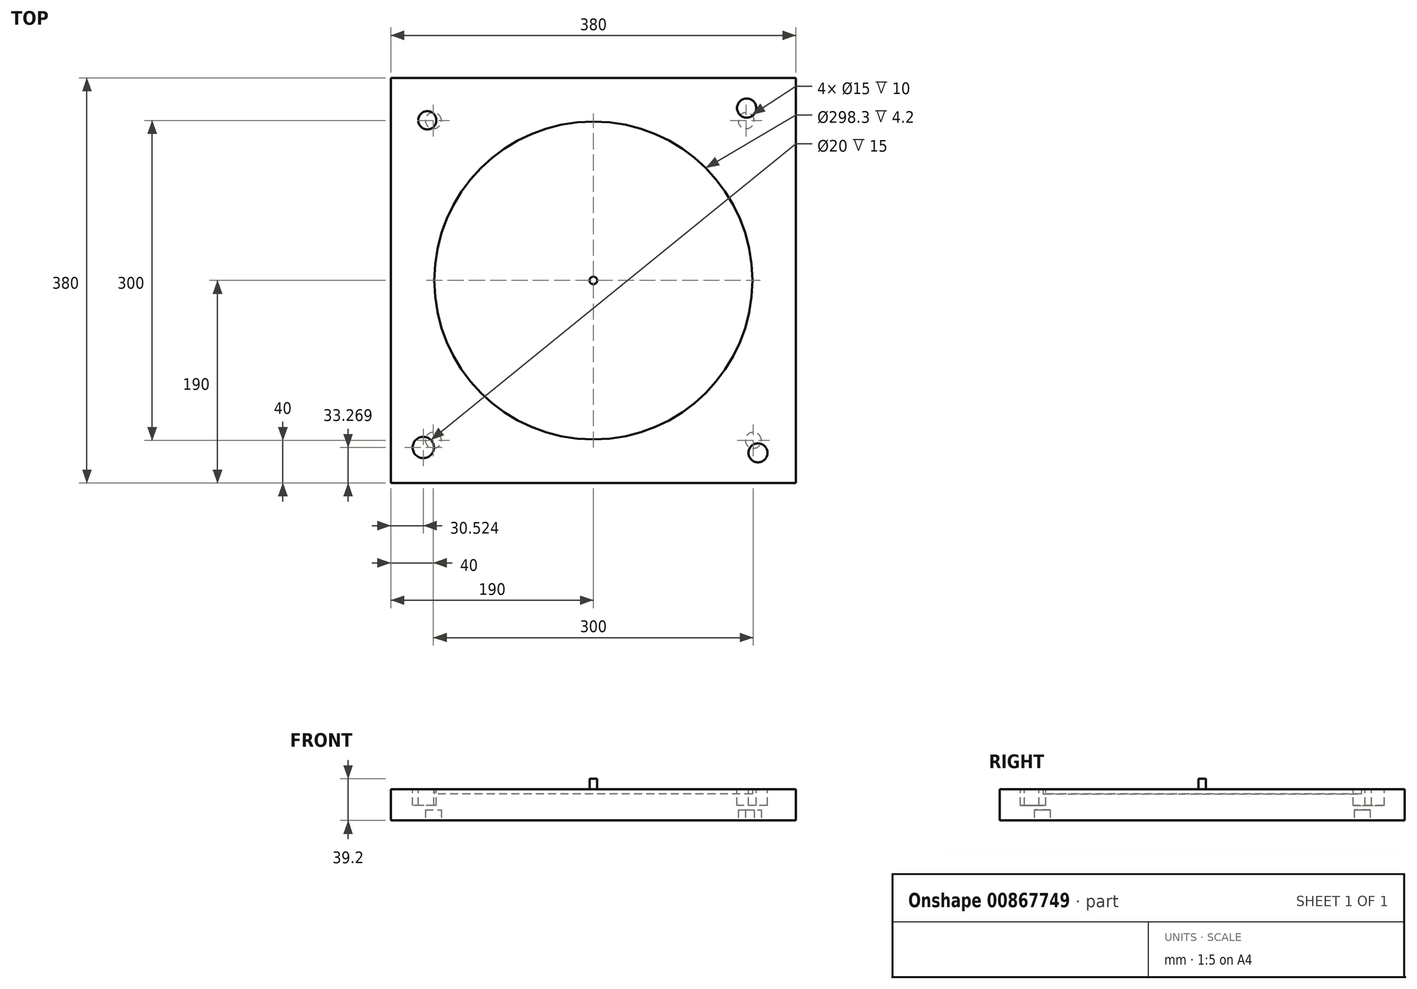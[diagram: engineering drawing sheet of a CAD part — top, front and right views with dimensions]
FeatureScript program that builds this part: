
annotation { "Feature Type Name" : "Feature", "Feature Type Description" : "" }
export const myFeature = defineFeature(function(context is Context, id is Id, definition is map)
    precondition{}
    {
        {
            var Q0;
            Q0=qCreatedBy(makeId("Top.planeOp"),FACE);
            var sketch = newSketch(context, id + "F0", { "sketchPlane" : qUnion([Q0])});
            skLineSegment(sketch, "E0.bottom", {"start": v(-190, 190) * mm, "end": v(190, 190) * mm});
            skLineSegment(sketch, "E0.top", {"start": v(-190, -190) * mm, "end": v(190, -190) * mm});
            skLineSegment(sketch, "E0.left", {"start": v(-190, 190) * mm, "end": v(-190, -190) * mm});
            skLineSegment(sketch, "E0.right", {"start": v(190, 190) * mm, "end": v(190, -190) * mm});
            skPoint(sketch, "E0.middle", {"position": v(0, 0) * mm});
            skSolve(sketch);
        }
        {
            var Q0;
            Q0=makeQuery(id+"F0.imprint","IMPRINT",FACE,{"disambiguationData":[TD([[makeQuery(id+"F0.imprint","IMPRINT",EDGE,{"derivedFrom":sQuery(id+"F0.wireOp",EDGE,"E0.bottom")}),-1.0]])]});
            var sketch = newSketch(context, id + "F1", { "sketchPlane" : qUnion([Q0])});
            skCircle(sketch, "E1", {"center": v(0, 0) * mm, "radius": 149.15 * mm});
            skCircle(sketch, "E2", {"center": v(0, 0) * mm, "radius": 3.6 * mm});
            skSolve(sketch);
        }
        {
            var Q0;
            Q0=makeQuery(id+"F0.imprint","IMPRINT",FACE,{"disambiguationData":[TD([[makeQuery(id+"F0.imprint","IMPRINT",EDGE,{"derivedFrom":sQuery(id+"F0.wireOp",EDGE,"E0.bottom")}),-1.0]])]});
            extrude(context, id + "F2", {"entities" : qUnion([Q0]), "depth" : 25 * mm, "offsetDistance" : 25 * mm});
        }
        {
            var Q0;
            Q0=makeQuery(id+"F1.imprint","IMPRINT",FACE,{"disambiguationData":[TD([[makeQuery(id+"F1.imprint","IMPRINT",EDGE,{"derivedFrom":sQuery(id+"F1.wireOp",EDGE,"E1")}),1.0]])]});
            extrude(context, id + "F3", {"entities" : qUnion([Q0]), "operationType" : NewBodyOperationType.ADD, "depth" : 4.2 * mm, "offsetDistance" : 25 * mm});
        }
        {
            var Q0;
            Q0=makeQuery(id+"F2.opExtrude","CAP_FACE",FACE,{"disambiguationData":[OSD([sQuery(id+"F0.wireOp",EDGE,"E0.bottom"),sQuery(id+"F0.wireOp",EDGE,"E0.top"),sQuery(id+"F0.wireOp",EDGE,"E0.left"),sQuery(id+"F0.wireOp",EDGE,"E0.right")])],"isStart":false});
            var sketch = newSketch(context, id + "F4", { "sketchPlane" : qUnion([Q0])});
            skCircle(sketch, "E3", {"center": v(0, 0) * mm, "radius": 149.15 * mm});
            skSolve(sketch);
        }
        {
            var Q0;
            Q0=makeQuery(id+"F4.imprint","IMPRINT",FACE,{"disambiguationData":[TD([[makeQuery(id+"F4.imprint","IMPRINT",EDGE,{"derivedFrom":sQuery(id+"F4.wireOp",EDGE,"E3")}),-1.0]])]});
            extrude(context, id + "F5", {"entities" : qUnion([Q0]), "operationType" : NewBodyOperationType.ADD, "depth" : 4.2 * mm, "offsetDistance" : 25 * mm});
        }
        {
            var Q0;
            Q0=makeQuery(id+"F5.opExtrude","CAP_FACE",FACE,{"disambiguationData":[OSD([sQuery(id+"F0.wireOp",EDGE,"E0.bottom"),sQuery(id+"F0.wireOp",EDGE,"E0.top"),sQuery(id+"F0.wireOp",EDGE,"E0.left"),sQuery(id+"F0.wireOp",EDGE,"E0.right"),sQuery(id+"F4.wireOp",EDGE,"E3")])],"isStart":false});
            var sketch = newSketch(context, id + "F6", { "sketchPlane" : qUnion([Q0])});
            skCircle(sketch, "E4", {"center": v(0, 0) * mm, "radius": 3.6 * mm});
            skSolve(sketch);
        }
        {
            var Q0;
            Q0=makeQuery(id+"F2.opExtrude","CAP_FACE",FACE,{"disambiguationData":[OSD([sQuery(id+"F0.wireOp",EDGE,"E0.bottom"),sQuery(id+"F0.wireOp",EDGE,"E0.top"),sQuery(id+"F0.wireOp",EDGE,"E0.left"),sQuery(id+"F0.wireOp",EDGE,"E0.right")])],"isStart":true});
            var sketch = newSketch(context, id + "F7", { "sketchPlane" : qUnion([Q0])});
            skCircle(sketch, "E5", {"center": v(-150, 150) * mm, "radius": 7.5 * mm});
            skCircle(sketch, "E6", {"center": v(-150, -150) * mm, "radius": 7.5 * mm});
            skCircle(sketch, "E7", {"center": v(143.27, -150) * mm, "radius": 7.5 * mm});
            skCircle(sketch, "E8", {"center": v(150, 150) * mm, "radius": 7.5 * mm});
            skSolve(sketch);
        }
        {
            var Q0;
            Q0=makeQuery(id+"F7.imprint","IMPRINT",FACE,{"disambiguationData":[TD([[makeQuery(id+"F7.imprint","IMPRINT",EDGE,{"derivedFrom":sQuery(id+"F7.wireOp",EDGE,"E5")}),1.0]])]});
            var Q1;
            Q1=makeQuery(id+"F7.imprint","IMPRINT",FACE,{"disambiguationData":[TD([[makeQuery(id+"F7.imprint","IMPRINT",EDGE,{"derivedFrom":sQuery(id+"F7.wireOp",EDGE,"E6")}),1.0]])]});
            var Q2;
            Q2=makeQuery(id+"F7.imprint","IMPRINT",FACE,{"disambiguationData":[TD([[makeQuery(id+"F7.imprint","IMPRINT",EDGE,{"derivedFrom":sQuery(id+"F7.wireOp",EDGE,"E7")}),1.0]])]});
            var Q3;
            Q3=makeQuery(id+"F7.imprint","IMPRINT",FACE,{"disambiguationData":[TD([[makeQuery(id+"F7.imprint","IMPRINT",EDGE,{"derivedFrom":sQuery(id+"F7.wireOp",EDGE,"E8")}),1.0]])]});
            extrude(context, id + "F8", {"entities" : qUnion([Q0, Q1, Q2, Q3]), "operationType" : NewBodyOperationType.REMOVE, "oppositeDirection" : true, "depth" : 10 * mm, "offsetDistance" : 25 * mm});
        }
        {
            var Q0;
            Q0=makeQuery(id+"F5.opExtrude","CAP_FACE",FACE,{"disambiguationData":[OSD([sQuery(id+"F0.wireOp",EDGE,"E0.bottom"),sQuery(id+"F0.wireOp",EDGE,"E0.top"),sQuery(id+"F0.wireOp",EDGE,"E0.left"),sQuery(id+"F0.wireOp",EDGE,"E0.right"),sQuery(id+"F4.wireOp",EDGE,"E3")])],"isStart":false});
            var sketch = newSketch(context, id + "F9", { "sketchPlane" : qUnion([Q0])});
            skCircle(sketch, "E9", {"center": v(-155.69, 150.3) * mm, "radius": 8.55 * mm});
            skCircle(sketch, "E10", {"center": v(143.75, 161.76) * mm, "radius": 9 * mm});
            skCircle(sketch, "E11", {"center": v(154.38, -161.76) * mm, "radius": 8.88 * mm});
            skCircle(sketch, "E12", {"center": v(-159.48, -156.73) * mm, "radius": 10 * mm});
            skSolve(sketch);
        }
        {
            var Q0;
            Q0=makeQuery(id+"F9.imprint","IMPRINT",FACE,{"disambiguationData":[TD([[makeQuery(id+"F9.imprint","IMPRINT",EDGE,{"derivedFrom":sQuery(id+"F9.wireOp",EDGE,"E9")}),1.0]])]});
            var Q1;
            Q1=makeQuery(id+"F9.imprint","IMPRINT",FACE,{"disambiguationData":[TD([[makeQuery(id+"F9.imprint","IMPRINT",EDGE,{"derivedFrom":sQuery(id+"F9.wireOp",EDGE,"E10")}),1.0]])]});
            var Q2;
            Q2=makeQuery(id+"F9.imprint","IMPRINT",FACE,{"disambiguationData":[TD([[makeQuery(id+"F9.imprint","IMPRINT",EDGE,{"derivedFrom":sQuery(id+"F9.wireOp",EDGE,"E11")}),1.0]])]});
            var Q3;
            Q3=makeQuery(id+"F9.imprint","IMPRINT",FACE,{"disambiguationData":[TD([[makeQuery(id+"F9.imprint","IMPRINT",EDGE,{"derivedFrom":sQuery(id+"F9.wireOp",EDGE,"E12")}),1.0]])]});
            extrude(context, id + "F10", {"entities" : qUnion([Q0, Q1, Q2, Q3]), "operationType" : NewBodyOperationType.REMOVE, "oppositeDirection" : true, "depth" : 15 * mm, "offsetDistance" : 25 * mm});
        }
        {
            var Q0;
            Q0 = qSketchRegion(id + "F6", true);
            extrude(context, id + "F11", {"entities" : qUnion([Q0]), "depth" : 10 * mm, "offsetDistance" : 25 * mm});
        }
    });
